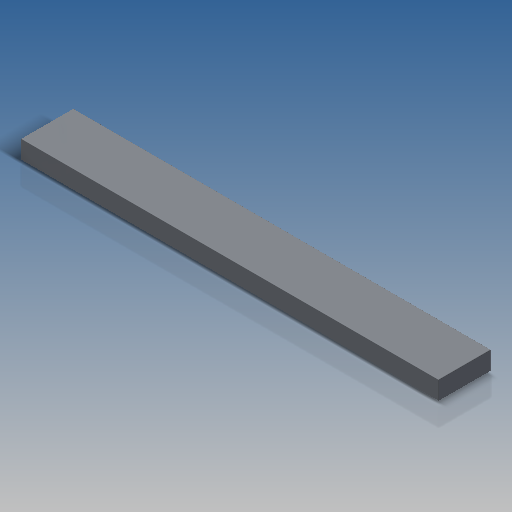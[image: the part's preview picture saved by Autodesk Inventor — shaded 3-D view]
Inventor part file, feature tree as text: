
AUTODESK INVENTOR PART (.ipt)
format: ipt  version: 2018.3 (Build 223284000, 284)  size: 188,416 bytes
history: native  units: in
note: dims shown in document units (in); Inventor stores cm internally (conversion verified against a paired STEP export)
features: extrude x4, sketch x2, other x2, pattern_linear x1, fillet x1
ambient origin geometry x8: Origin, YZ Plane, XZ Plane, XY Plane, X Axis, Y Axis, Z Axis, Center Point
bodies: Solid1 (feature_tree)
feature tree (10):
  extrude  "Extrusion1"  Depth=0.315in
  sketch  "Sketch3"  dims[d4=0.126in d5=0.0in d7=0.0591in d8=0.063in d11=0.063in d12=0.0in d22=0.0039in d60=0.2564in d61=0.189in d62=0.063in d75=0.315in d76=0.315in d86=0.126in d87=0.0709in d88=0.0in d89=2.7559in d91=0.315in d93=0.315in d94=0.0in d95=0.0in d96=0.0in d97=0.0in d98=0.0in d99=0.0157in d100=0.0157in d101=0.0157in d102=0.0in]
  extrude  "Extrusion2"  Depth=0.063in
  extrude  "Extrusion7"  Depth=0.063in TaperAngle=0.0deg
  extrude  "Extrusion6"  Depth=0.0039in
  pattern_linear  "Rectangular Pattern3"  Spacing1=0.2564in  [1 undecoded]
  fillet  "Fillet1"  Radius=0.189in
  other  "Work Axis1"
  other  "Work Axis2"
  sketch  "Sketch2"  dims[d0=2.5197in d1=0.315in]
note: 1 required parameter value undecoded (feature->parameter linkage not recoverable at this tier; creation-order binding heuristic only, values carry confidence <= 0.55)
